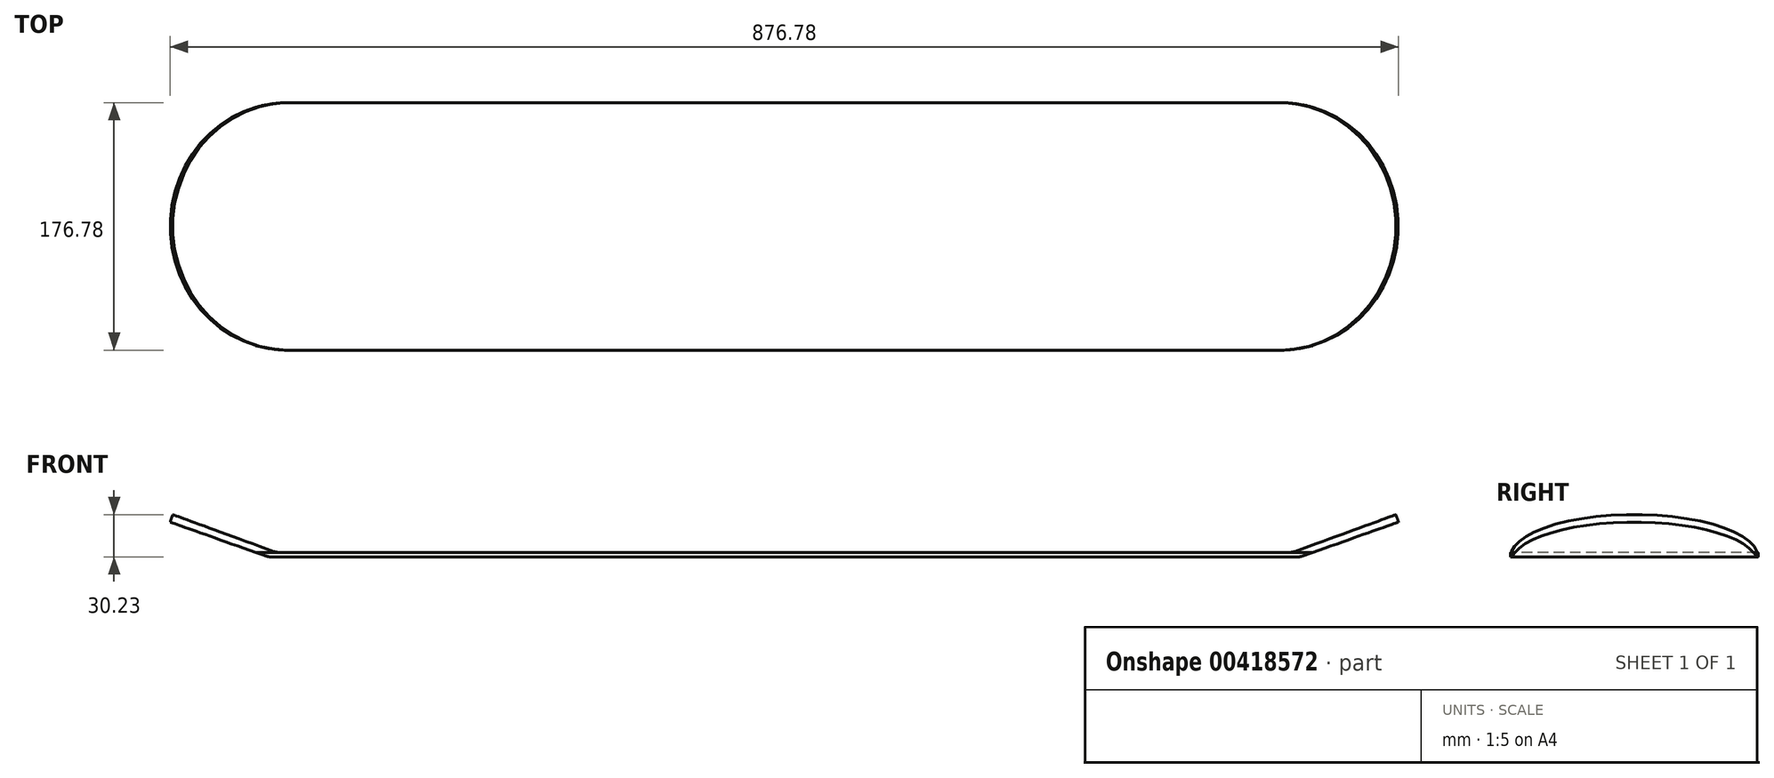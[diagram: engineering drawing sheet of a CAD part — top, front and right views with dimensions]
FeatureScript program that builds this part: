
annotation { "Feature Type Name" : "Feature", "Feature Type Description" : "" }
export const myFeature = defineFeature(function(context is Context, id is Id, definition is map)
    precondition{}
    {
        {
            var Q0;
            Q0=qCreatedBy(makeId("Top.planeOp"),FACE);
            var sketch = newSketch(context, id + "F0", { "sketchPlane" : qUnion([Q0])});
            skLineSegment(sketch, "E0.bottom", {"start": v(353.57, -88.4) * mm, "end": v(-353.57, -88.4) * mm});
            skLineSegment(sketch, "E0.top", {"start": v(353.57, 88.4) * mm, "end": v(-353.57, 88.4) * mm});
            skLineSegment(sketch, "E0.left", {"start": v(353.57, -88.4) * mm, "end": v(353.57, 88.4) * mm});
            skLineSegment(sketch, "E0.right", {"start": v(-353.57, -88.4) * mm, "end": v(-353.57, 88.4) * mm});
            skPoint(sketch, "E0.middle", {"position": v(0, 0) * mm});
            skCircle(sketch, "E1", {"center": v(353.57, 0) * mm, "radius": 88.4 * mm});
            skSolve(sketch);
        }
        {
            var Q0;
            Q0=qSketchRegion(id+"F0",true);
            extrude(context, id + "F1", {"entities" : qUnion([Q0]), "depth" : 3.17 * mm});
        }
        {
            var Q0;
            Q0=makeQuery(id+"F1.opExtrude","CAP_FACE",FACE,{"disambiguationData":[OSD([sQuery(id+"F0.wireOp",EDGE,"E0.bottom"),sQuery(id+"F0.wireOp",EDGE,"E0.top"),sQuery(id+"F0.wireOp",EDGE,"E0.right"),sQuery(id+"F0.wireOp",EDGE,"E1")])],"isStart":false});
            var sketch = newSketch(context, id + "F2", { "sketchPlane" : qUnion([Q0])});
            skLineSegment(sketch, "E2", {"start": v(353.57, 88.4) * mm, "end": v(353.57, -88.4) * mm});
            skPoint(sketch, "E3.endSnap0", {"position": v(-353.57, 0) * mm});
            skLineSegment(sketch, "E4", {"start": v(-265.18, 88.4) * mm, "end": v(-265.18, -88.4) * mm});
            skArc(sketch, "E5", {"start": v(-265.18, 88.4) * mm, "mid": v(-353.57, 0) * mm, "end": v(-265.18, -88.4) * mm});
            skSolve(sketch);
        }
        {
            var Q0;
            {var subQ1=makeQuery(id+"F1.opExtrude","CAP_EDGE",EDGE,{"disambiguationData":[OSD([sQuery(id+"F0.wireOp",EDGE,"E0.top")])],"isStart":false});var subQ3=makeQuery(id+"F1.opExtrude","CAP_EDGE",EDGE,{"disambiguationData":[OSD([sQuery(id+"F0.wireOp",EDGE,"E0.right")])],"isStart":false});var subQ5=makeQuery(id+"F2.imprint","INTERSECT",VERTEX,{"derivedFrom":[subQ1,subQ3]});Q0=makeQuery(id+"F2.imprint","IMPRINT",FACE,{"disambiguationData":[TD([[makeQuery(id+"F2.imprint","IMPRINT",EDGE,{"disambiguationData":[TD([[subQ5,1.0]])],"derivedFrom":subQ3}),-1.0]])]});}
            var Q1;
            {var subQ1=makeQuery(id+"F1.opExtrude","CAP_EDGE",EDGE,{"disambiguationData":[OSD([sQuery(id+"F0.wireOp",EDGE,"E0.bottom")])],"isStart":false});var subQ3=makeQuery(id+"F1.opExtrude","CAP_EDGE",EDGE,{"disambiguationData":[OSD([sQuery(id+"F0.wireOp",EDGE,"E0.right")])],"isStart":false});var subQ5=makeQuery(id+"F2.imprint","INTERSECT",VERTEX,{"derivedFrom":[subQ1,subQ3]});Q1=makeQuery(id+"F2.imprint","IMPRINT",FACE,{"disambiguationData":[TD([[makeQuery(id+"F2.imprint","IMPRINT",EDGE,{"disambiguationData":[TD([[subQ5,-1.0]])],"derivedFrom":subQ3}),-1.0]])]});}
            extrude(context, id + "F3", {"entities" : qUnion([Q0, Q1]), "operationType" : NewBodyOperationType.REMOVE, "oppositeDirection" : true, "depth" : 25.4 * mm, "hasSecondDirection" : true, "secondDirectionOppositeDirection" : false, "secondDirectionDepth" : 50.8 * mm});
        }
        {
            var Q0;
            {var subQ0=sQuery(id+"F0.wireOp",EDGE,"E0.left");Q0=makeQuery(id+"F0.imprint","IMPRINT",FACE,{"disambiguationData":[TD([[makeQuery(id+"F0.imprint","IMPRINT",EDGE,{"derivedFrom":subQ0}),-1.0]])]});}
            var Q1;
            Q1=sQuery(id+"F0.wireOp",EDGE,"E0.left");
            revolve(context, id + "F4", {"entities" : qUnion([Q0]), "axis" : qUnion([Q1]), "revolveType" : RevolveType.ONE_DIRECTION, "oppositeDirection" : true, "angle" : 20 * degree});
        }
        {
            var Q0;
            Q0=qCreatedBy(makeId("Front.planeOp"),FACE);
            var sketch = newSketch(context, id + "F5", { "sketchPlane" : qUnion([Q0])});
            skLineSegment(sketch, "E6", {"start": v(356.56, -4.08) * mm, "end": v(450.25, 29.07) * mm});
            skLineSegment(sketch, "E7", {"start": v(450.25, 29.07) * mm, "end": v(450.25, -5.04) * mm});
            skLineSegment(sketch, "E8", {"start": v(450.25, -5.04) * mm, "end": v(356.56, -4.08) * mm});
            skSolve(sketch);
        }
        {
            var Q0;
            Q0 = qSketchRegion(id + "F5", true);
            extrude(context, id + "F6", {"entities" : qUnion([Q0]), "operationType" : NewBodyOperationType.REMOVE, "endBound" : BoundingType.SYMMETRIC, "oppositeDirection" : true, "depth" : 176.78 * mm});
        }
        {
            var Q0;
            Q0=makeQuery(id+"F1.opExtrude","SWEPT_BODY",BODY,{"disambiguationData":[OSD([sQuery(id+"F0.wireOp",EDGE,"E0.bottom"),sQuery(id+"F0.wireOp",EDGE,"E0.top"),sQuery(id+"F0.wireOp",EDGE,"E0.right"),sQuery(id+"F0.wireOp",EDGE,"E1")])]});
            var Q1;
            Q1=makeQuery(id+"F4.opRevolve","SWEPT_BODY",BODY,{"disambiguationData":[OSD([sQuery(id+"F0.wireOp",EDGE,"E0.left"),sQuery(id+"F0.wireOp",EDGE,"E1")])]});
            var Q2;
            Q2=qCreatedBy(makeId("Right.planeOp"),FACE);
            mirror(context, id + "F7", {"operationType" : NewBodyOperationType.ADD, "entities" : qUnion([Q0, Q1]), "mirrorPlane" : qUnion([Q2])});
        }
        {
            var Q0;
            Q0=makeQuery(id+"F6.boolean.opBoolean","INTERSECT",EDGE,{"derivedFrom":[makeQuery(id+"F1.opExtrude","CAP_FACE",FACE,{"disambiguationData":[OSD([sQuery(id+"F0.wireOp",EDGE,"E0.bottom"),sQuery(id+"F0.wireOp",EDGE,"E0.top"),sQuery(id+"F0.wireOp",EDGE,"E0.right"),sQuery(id+"F0.wireOp",EDGE,"E1")])],"isStart":true}),makeQuery(id+"F6.opExtrude","SWEPT_FACE",FACE,{"disambiguationData":[OSD([sQuery(id+"F5.wireOp",EDGE,"E6")])]})]});
            var Q1;
            Q1=makeQuery(id+"F7.opPattern","COPY",EDGE,{"derivedFrom":makeQuery(id+"F6.boolean.opBoolean","INTERSECT",EDGE,{"derivedFrom":[makeQuery(id+"F1.opExtrude","CAP_FACE",FACE,{"disambiguationData":[OSD([sQuery(id+"F0.wireOp",EDGE,"E0.bottom"),sQuery(id+"F0.wireOp",EDGE,"E0.top"),sQuery(id+"F0.wireOp",EDGE,"E0.right"),sQuery(id+"F0.wireOp",EDGE,"E1")])],"isStart":true}),makeQuery(id+"F6.opExtrude","SWEPT_FACE",FACE,{"disambiguationData":[OSD([sQuery(id+"F5.wireOp",EDGE,"E6")])]})]}),"instanceName":"1"});
            fillet(context, id + "F8", {"entities" : qUnion([Q0, Q1]), "radius" : 12.7 * mm, "tangentPropagation" : true, "allowEdgeOverflow" : false});
        }
        {
            var Q0;
            {var subQ0=sQuery(id+"F0.wireOp",EDGE,"E1");Q0=makeQuery(id+"F7.boolean.opBoolean","INTERSECT",EDGE,{"derivedFrom":[makeQuery(id+"F7.opPattern","COPY",FACE,{"derivedFrom":makeQuery(id+"F4.opRevolve","CAP_FACE",FACE,{"disambiguationData":[OSD([sQuery(id+"F0.wireOp",EDGE,"E0.left"),subQ0])],"isStart":false}),"instanceName":"1"}),makeQuery(id+"F7.opPattern","COPY",FACE,{"derivedFrom":makeQuery(id+"F1.opExtrude","CAP_FACE",FACE,{"disambiguationData":[OSD([sQuery(id+"F0.wireOp",EDGE,"E0.bottom"),sQuery(id+"F0.wireOp",EDGE,"E0.top"),sQuery(id+"F0.wireOp",EDGE,"E0.right"),subQ0])],"isStart":false}),"instanceName":"1"})]});}
            var Q1;
            {var subQ0=sQuery(id+"F0.wireOp",EDGE,"E1");var subQ1=makeQuery(id+"F1.opExtrude","CAP_FACE",FACE,{"disambiguationData":[OSD([sQuery(id+"F0.wireOp",EDGE,"E0.bottom"),sQuery(id+"F0.wireOp",EDGE,"E0.top"),sQuery(id+"F0.wireOp",EDGE,"E0.right"),subQ0])],"isStart":false});Q1=makeQuery(id+"F7.boolean.opBoolean","INTERSECT",EDGE,{"derivedFrom":[makeQuery(id+"F4.opRevolve","CAP_FACE",FACE,{"disambiguationData":[OSD([sQuery(id+"F0.wireOp",EDGE,"E0.left"),subQ0])],"isStart":false}),subQ1,makeQuery(id+"F7.opPattern","COPY",FACE,{"derivedFrom":subQ1,"instanceName":"1"})]});}
            fillet(context, id + "F9", {"entities" : qUnion([Q0, Q1]), "radius" : 12.7 * mm, "tangentPropagation" : true, "allowEdgeOverflow" : false});
        }
    });
